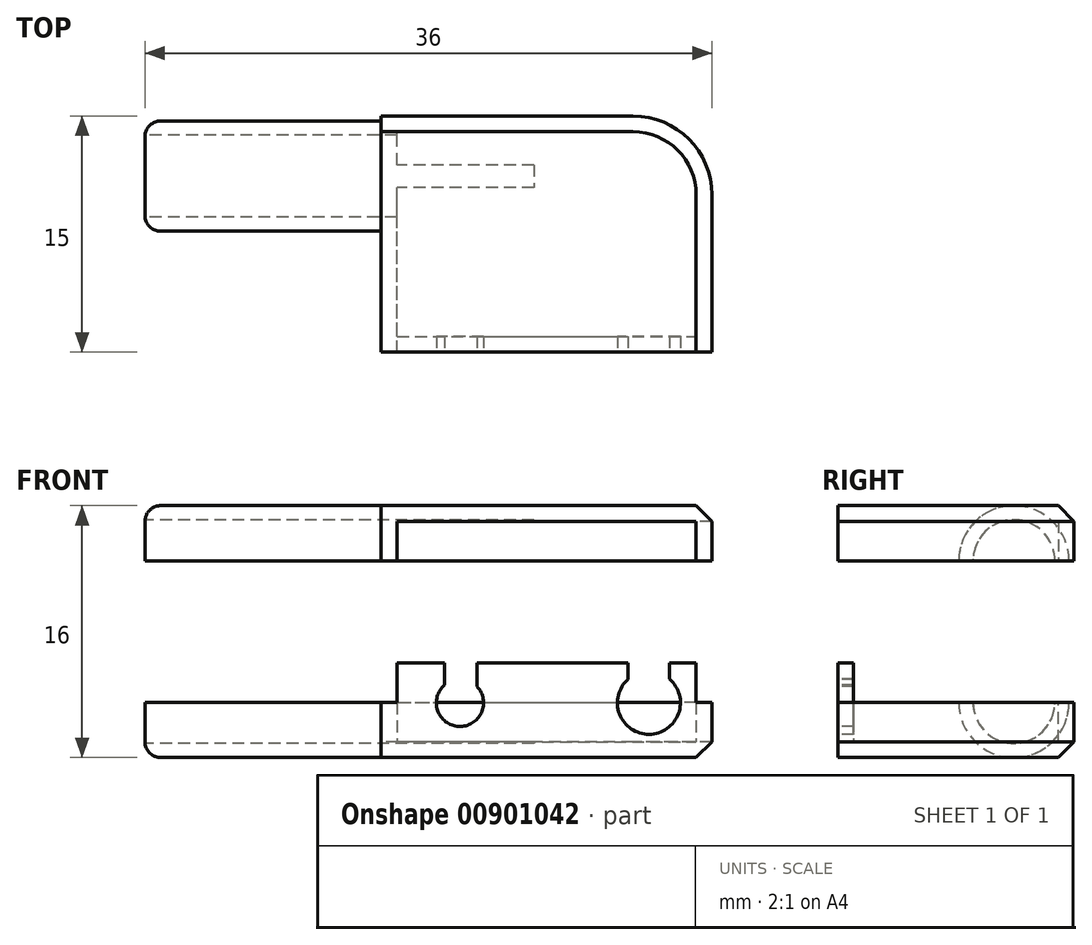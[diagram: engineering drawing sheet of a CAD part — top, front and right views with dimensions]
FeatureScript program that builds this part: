
annotation { "Feature Type Name" : "Feature", "Feature Type Description" : "" }
export const myFeature = defineFeature(function(context is Context, id is Id, definition is map)
    precondition{}
    {
        {
            var Q0;
            Q0=qCreatedBy(makeId("Top.planeOp"),FACE);
            var sketch = newSketch(context, id + "F0", { "sketchPlane" : qUnion([Q0])});
            skLineSegment(sketch, "E0.bottom", {"start": v(-8.48, -5.17) * mm, "end": v(12.52, -5.17) * mm});
            skLineSegment(sketch, "E0.top", {"start": v(-8.48, 9.83) * mm, "end": v(7.52, 9.83) * mm});
            skLineSegment(sketch, "E0.left", {"start": v(-8.48, -5.17) * mm, "end": v(-8.48, 9.83) * mm});
            skLineSegment(sketch, "E0.right", {"start": v(12.52, -5.17) * mm, "end": v(12.52, 4.83) * mm});
            skPoint(sketch, "E1.visualSharp", {"position": v(12.52, 9.83) * mm});
            skArc(sketch, "E1.filletArc", {"start": v(12.52, 4.83) * mm, "mid": v(11.05, 8.36) * mm, "end": v(7.52, 9.83) * mm});
            skSolve(sketch);
        }
        {
            var Q0;
            Q0=makeQuery(id+"F0.imprint","IMPRINT",FACE,{"disambiguationData":[TD([[makeQuery(id+"F0.imprint","IMPRINT",EDGE,{"derivedFrom":sQuery(id+"F0.wireOp",EDGE,"E0.bottom")}),1.0]])]});
            extrude(context, id + "F1", {"entities" : qUnion([Q0]), "depth" : 3.5 * mm, "offsetDistance" : 25 * mm});
        }
        {
            var Q0;
            Q0=makeQuery(id+"F1.opExtrude","CAP_FACE",FACE,{"disambiguationData":[OSD([sQuery(id+"F0.wireOp",EDGE,"E0.bottom"),sQuery(id+"F0.wireOp",EDGE,"E0.top"),sQuery(id+"F0.wireOp",EDGE,"E0.left"),sQuery(id+"F0.wireOp",EDGE,"E0.right"),sQuery(id+"F0.wireOp",EDGE,"E1.filletArc")])],"isStart":false});
            var sketch = newSketch(context, id + "F2", { "sketchPlane" : qUnion([Q0])});
            skLineSegment(sketch, "E2.0", {"start": v(11.52, -5.17) * mm, "end": v(11.52, 4.83) * mm});
            skArc(sketch, "E2.1", {"start": v(11.52, 4.83) * mm, "mid": v(10.35, 7.65) * mm, "end": v(7.52, 8.83) * mm});
            skLineSegment(sketch, "E2.2", {"start": v(-7.48, 8.83) * mm, "end": v(7.52, 8.83) * mm});
            skLineSegment(sketch, "E2.3", {"start": v(-7.48, -5.17) * mm, "end": v(-7.48, 8.83) * mm});
            skSolve(sketch);
        }
        {
            var Q0;
            {var subQ1=sQuery(id+"F2.wireOp",EDGE,"E2.0");Q0=makeQuery(id+"F2.imprint","IMPRINT",FACE,{"disambiguationData":[TD([[makeQuery(id+"F2.imprint","IMPRINT",EDGE,{"derivedFrom":subQ1}),1.0]])]});}
            extrude(context, id + "F3", {"entities" : qUnion([Q0]), "operationType" : NewBodyOperationType.REMOVE, "oppositeDirection" : true, "depth" : 2.5 * mm, "offsetDistance" : 25 * mm});
        }
        {
            var Q0;
            Q0=makeQuery(id+"F1.opExtrude","SWEPT_FACE",FACE,{"disambiguationData":[OSD([sQuery(id+"F0.wireOp",EDGE,"E0.left")])]});
            var sketch = newSketch(context, id + "F4", { "sketchPlane" : qUnion([Q0])});
            skCircle(sketch, "E3", {"center": v(-6.01, 3.5) * mm, "radius": 2.6 * mm});
            skSolve(sketch);
        }
        {
            var Q0;
            {var subQ0=sQuery(id+"F4.wireOp",EDGE,"E3");var subQ1=makeQuery(id+"F1.opExtrude","CAP_EDGE",EDGE,{"disambiguationData":[OSD([sQuery(id+"F0.wireOp",EDGE,"E0.left")])],"isStart":false});var subQ2=makeQuery(id+"F4.imprint","INTERSECT",VERTEX,{"disambiguationData":[OD(0.0)],"derivedFrom":[subQ1,subQ0]});Q0=makeQuery(id+"F4.imprint","IMPRINT",FACE,{"disambiguationData":[TD([[makeQuery(id+"F4.imprint","IMPRINT",EDGE,{"disambiguationData":[TD([[subQ2,1.0]])],"derivedFrom":subQ0}),1.0]])]});}
            extrude(context, id + "F5", {"entities" : qUnion([Q0]), "operationType" : NewBodyOperationType.REMOVE, "oppositeDirection" : true, "depth" : 9.7 * mm, "offsetDistance" : 25 * mm});
        }
        {
            var Q0;
            Q0=makeQuery(id+"F1.opExtrude","SWEPT_FACE",FACE,{"disambiguationData":[OSD([sQuery(id+"F0.wireOp",EDGE,"E0.left")])]});
            var sketch = newSketch(context, id + "F6", { "sketchPlane" : qUnion([Q0])});
            skCircle(sketch, "E4", {"center": v(-6.01, 3.5) * mm, "radius": 2.6 * mm});
            skCircle(sketch, "E5", {"center": v(-6.01, 3.5) * mm, "radius": 3.5 * mm});
            skSolve(sketch);
        }
        {
            var Q0;
            {var subQ2=sQuery(id+"F0.wireOp",EDGE,"E0.left");var subQ10=sQuery(id+"F6.wireOp",EDGE,"E5");var subQ12=makeQuery(id+"F6.imprint","INTERSECT",VERTEX,{"derivedFrom":[makeQuery(id+"F1.opExtrude","CAP_EDGE",EDGE,{"disambiguationData":[OSD([subQ2])],"isStart":true}),subQ10]});Q0=makeQuery(id+"F6.imprint","IMPRINT",FACE,{"disambiguationData":[TD([[makeQuery(id+"F6.imprint","IMPRINT",EDGE,{"disambiguationData":[TD([[subQ12,1.0]])],"derivedFrom":subQ10}),1.0]])]});}
            extrude(context, id + "F7", {"entities" : qUnion([Q0]), "operationType" : NewBodyOperationType.ADD, "depth" : 15 * mm, "offsetDistance" : 25 * mm});
        }
        {
            var Q0;
            Q0=makeQuery(id+"F7.opExtrude","CAP_EDGE",EDGE,{"disambiguationData":[OSD([sQuery(id+"F6.wireOp",EDGE,"E5")])],"isStart":false});
            fillet(context, id + "F8", {"entities" : qUnion([Q0]), "radius" : 1 * mm, "tangentPropagation" : true, "allowEdgeOverflow" : false});
        }
        {
            var Q0;
            Q0=makeQuery(id+"F1.opExtrude","CAP_EDGE",EDGE,{"disambiguationData":[OSD([sQuery(id+"F0.wireOp",EDGE,"E0.right")])],"isStart":true});
            var Q1;
            Q1=makeQuery(id+"F1.opExtrude","CAP_EDGE",EDGE,{"disambiguationData":[OSD([sQuery(id+"F0.wireOp",EDGE,"E1.filletArc")])],"isStart":true});
            var Q2;
            Q2=makeQuery(id+"F1.opExtrude","CAP_EDGE",EDGE,{"disambiguationData":[OSD([sQuery(id+"F0.wireOp",EDGE,"E0.top")])],"isStart":true});
            chamfer(context, id + "F9", {"entities" : qUnion([Q0, Q1, Q2]), "width" : 1 * mm, "tangentPropagation" : true});
        }
        {
            var Q0;
            Q0=makeQuery(id+"F1.opExtrude","SWEPT_BODY",BODY,{"disambiguationData":[OSD([sQuery(id+"F0.wireOp",EDGE,"E0.bottom"),sQuery(id+"F0.wireOp",EDGE,"E0.top"),sQuery(id+"F0.wireOp",EDGE,"E0.left"),sQuery(id+"F0.wireOp",EDGE,"E0.right"),sQuery(id+"F0.wireOp",EDGE,"E1.filletArc")])]});
            var Q1;
            Q1=makeQuery(id+"F1.opExtrude","CAP_FACE",FACE,{"disambiguationData":[OSD([sQuery(id+"F0.wireOp",EDGE,"E0.bottom"),sQuery(id+"F0.wireOp",EDGE,"E0.top"),sQuery(id+"F0.wireOp",EDGE,"E0.left"),sQuery(id+"F0.wireOp",EDGE,"E0.right"),sQuery(id+"F0.wireOp",EDGE,"E1.filletArc")])],"isStart":true});
            mirror(context, id + "F10", {"entities" : qUnion([Q0]), "mirrorPlane" : qUnion([Q1])});
        }
        {
            var Q0;
            Q0=makeQuery(id+"F10.opPattern","COPY",BODY,{"derivedFrom":makeQuery(id+"F1.opExtrude","SWEPT_BODY",BODY,{"disambiguationData":[OSD([sQuery(id+"F0.wireOp",EDGE,"E0.bottom"),sQuery(id+"F0.wireOp",EDGE,"E0.top"),sQuery(id+"F0.wireOp",EDGE,"E0.left"),sQuery(id+"F0.wireOp",EDGE,"E0.right"),sQuery(id+"F0.wireOp",EDGE,"E1.filletArc")])]}),"instanceName":"1"});
            transform(context, id + "F11", {"entities" : qUnion([Q0]), "transformType" : TransformType.TRANSLATION_3D, "dx" : 0 * mm, "dy" : 0 * mm, "dz" : 16 * mm, "makeCopy" : false});
        }
        {
            var Q0;
            Q0=makeQuery(id+"F3.boolean.opBoolean","COPY",FACE,{"derivedFrom":makeQuery(id+"F3.opExtrude","CAP_FACE",FACE,{"disambiguationData":[OSD([sQuery(id+"F0.wireOp",EDGE,"E0.bottom"),sQuery(id+"F2.wireOp",EDGE,"E2.0"),sQuery(id+"F2.wireOp",EDGE,"E2.1"),sQuery(id+"F2.wireOp",EDGE,"E2.2"),sQuery(id+"F2.wireOp",EDGE,"E2.3")])],"isStart":false})});
            var Q1;
            Q1=qCreatedBy(makeId("Top.planeOp"),FACE);
            var sketch = newSketch(context, id + "F12", { "sketchPlane" : qUnion([Q0, Q1])});
            skLineSegment(sketch, "E6.bottom", {"start": v(-7.48, -5.17) * mm, "end": v(11.52, -5.17) * mm});
            skLineSegment(sketch, "E6.top", {"start": v(-7.48, -4.17) * mm, "end": v(11.52, -4.17) * mm});
            skLineSegment(sketch, "E6.left", {"start": v(-7.48, -5.17) * mm, "end": v(-7.48, -4.17) * mm});
            skLineSegment(sketch, "E6.right", {"start": v(11.52, -5.17) * mm, "end": v(11.52, -4.17) * mm});
            skSolve(sketch);
        }
        {
            var Q0;
            Q0 = qSketchRegion(id + "F12", true);
            extrude(context, id + "F13", {"entities" : qUnion([Q0]), "operationType" : NewBodyOperationType.ADD, "depth" : 5 * mm, "offsetDistance" : 25 * mm});
        }
        {
            var Q0;
            Q0=makeQuery(id+"F13.boolean.opBoolean","MERGE",FACE,{"derivedFrom":[makeQuery(id+"F1.opExtrude","SWEPT_FACE",FACE,{"disambiguationData":[OSD([sQuery(id+"F0.wireOp",EDGE,"E0.bottom")])]}),makeQuery(id+"F13.opExtrude","SWEPT_FACE",FACE,{"disambiguationData":[OSD([sQuery(id+"F12.wireOp",EDGE,"E6.bottom")])]})]});
            var sketch = newSketch(context, id + "F14", { "sketchPlane" : qUnion([Q0])});
            skSolve(sketch);
        }
        {
            var Q0;
            {var subQ0=sQuery(id+"F0.wireOp",EDGE,"E0.bottom");Q0=makeQuery(id+"F14.imprint","IMPRINT",FACE,{"disambiguationData":[TD([[makeQuery(id+"F14.imprint","IMPRINT",EDGE,{"derivedFrom":makeQuery(id+"F1.opExtrude","CAP_EDGE",EDGE,{"disambiguationData":[OSD([subQ0])],"isStart":true})}),1.0]])]});}
            var sketch = newSketch(context, id + "F15", { "sketchPlane" : qUnion([Q0])});
            skLineSegment(sketch, "E7", {"start": v(-5.97, 3.47) * mm, "end": v(12.54, 3.47) * mm, "construction": true});
            skCircle(sketch, "E8", {"center": v(-3.48, 3.47) * mm, "radius": 1.5 * mm});
            skCircle(sketch, "E9", {"center": v(8.52, 3.47) * mm, "radius": 2 * mm});
            skLineSegment(sketch, "E10.bottom", {"start": v(7.2, 6.05) * mm, "end": v(9.82, 6.05) * mm});
            skLineSegment(sketch, "E10.top", {"start": v(7.2, 4.08) * mm, "end": v(9.82, 4.08) * mm});
            skLineSegment(sketch, "E10.left", {"start": v(7.2, 6.05) * mm, "end": v(7.2, 4.08) * mm});
            skLineSegment(sketch, "E10.right", {"start": v(9.82, 6.05) * mm, "end": v(9.82, 4.08) * mm});
            skLineSegment(sketch, "E11.bottom", {"start": v(-4.45, 7.04) * mm, "end": v(-2.4, 7.04) * mm});
            skLineSegment(sketch, "E11.top", {"start": v(-4.45, 4.13) * mm, "end": v(-2.4, 4.13) * mm});
            skLineSegment(sketch, "E11.left", {"start": v(-4.45, 7.04) * mm, "end": v(-4.45, 4.13) * mm});
            skLineSegment(sketch, "E11.right", {"start": v(-2.4, 7.04) * mm, "end": v(-2.4, 4.13) * mm});
            skSolve(sketch);
        }
        {
            var Q0;
            Q0 = qSketchRegion(id + "F15", true);
            extrude(context, id + "F16", {"entities" : qUnion([Q0]), "operationType" : NewBodyOperationType.REMOVE, "oppositeDirection" : true, "depth" : 4 * mm, "offsetDistance" : 25 * mm});
        }
    });
